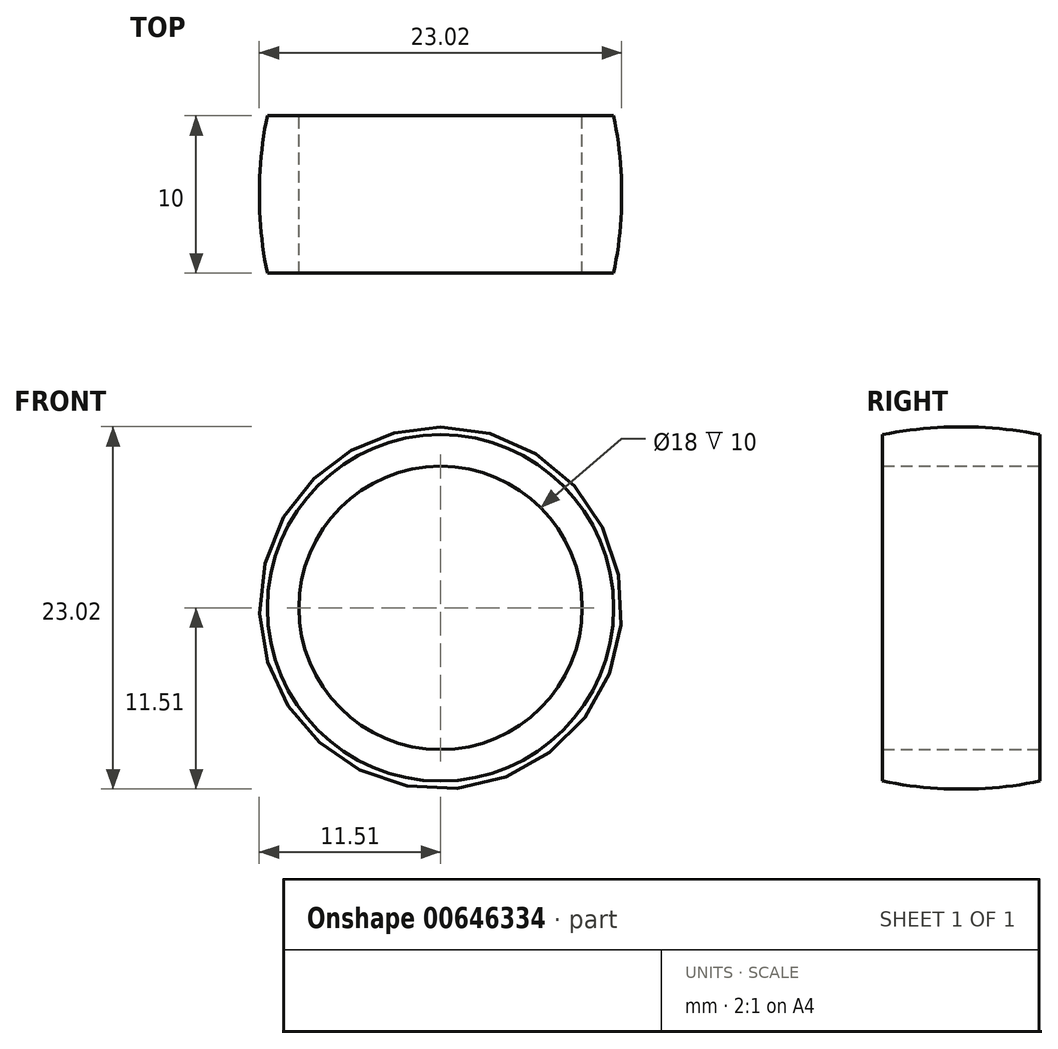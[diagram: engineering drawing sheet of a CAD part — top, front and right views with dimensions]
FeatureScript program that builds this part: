
annotation { "Feature Type Name" : "Feature", "Feature Type Description" : "" }
export const myFeature = defineFeature(function(context is Context, id is Id, definition is map)
    precondition{}
    {
        {
            var Q0;
            Q0=qCreatedBy(makeId("Top.planeOp"),FACE);
            var sketch = newSketch(context, id + "F0", { "sketchPlane" : qUnion([Q0])});
            skLineSegment(sketch, "E0", {"start": v(0, 0) * mm, "end": v(-9, 0) * mm, "construction": true});
            skLineSegment(sketch, "E1", {"start": v(-9, 5) * mm, "end": v(-9, -5) * mm});
            skLineSegment(sketch, "E2", {"start": v(-9, 5) * mm, "end": v(-11, 5) * mm});
            skLineSegment(sketch, "E3", {"start": v(-11, 5) * mm, "end": v(-9, 5) * mm});
            skLineSegment(sketch, "E4", {"start": v(-9, -5) * mm, "end": v(-11, -5) * mm});
            skArc(sketch, "E5", {"start": v(-11, 5) * mm, "mid": v(-11.5, 0) * mm, "end": v(-11, -5) * mm});
            skLineSegment(sketch, "E6", {"start": v(0, 0) * mm, "end": v(0, -6.28) * mm});
            skSolve(sketch);
        }
        {
            var Q0;
            Q0=makeQuery(id+"F0.imprint","IMPRINT",FACE,{"disambiguationData":[TD([[makeQuery(id+"F0.imprint","IMPRINT",EDGE,{"derivedFrom":sQuery(id+"F0.wireOp",EDGE,"E1")}),-1.0]])]});
            var Q1;
            Q1=sQuery(id+"F0.wireOp",EDGE,"E1");
            var Q2;
            Q2=sQuery(id+"F0.wireOp",EDGE,"E6");
            var Q3;
            Q3=sQuery(id+"F0.wireOp",EDGE,"E6");
            revolve(context, id + "F1", {"entities" : qUnion([Q0]), "surfaceEntities" : qUnion([Q1, Q2]), "axis" : qUnion([Q3]), "revolveType" : RevolveType.FULL});
        }
    });
